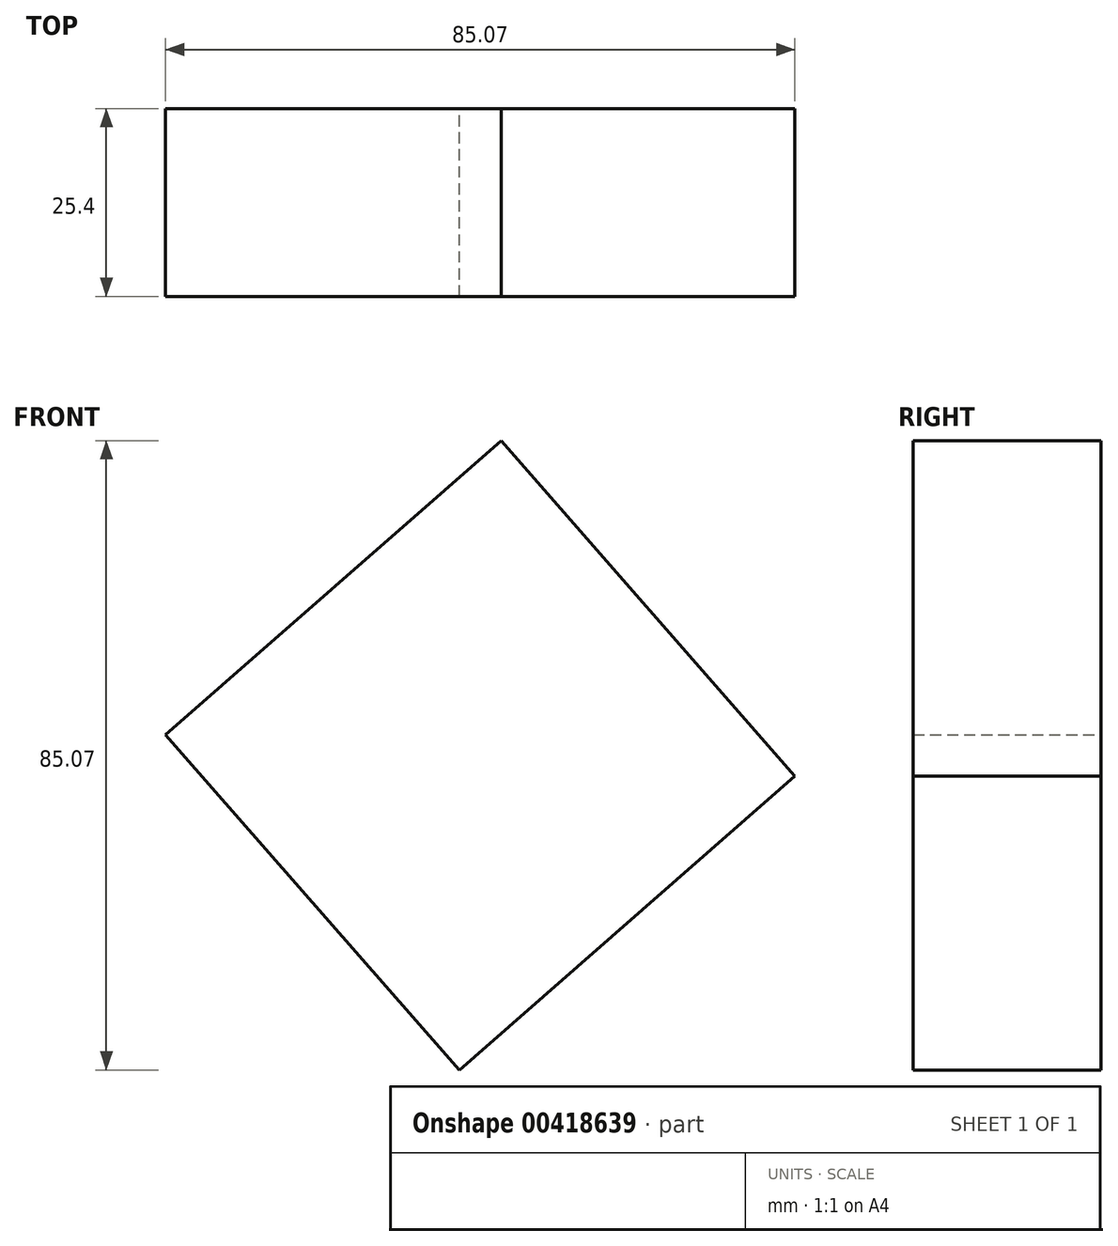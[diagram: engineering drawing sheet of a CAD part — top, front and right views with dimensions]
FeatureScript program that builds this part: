
annotation { "Feature Type Name" : "Feature", "Feature Type Description" : "" }
export const myFeature = defineFeature(function(context is Context, id is Id, definition is map)
    precondition{}
    {
        {
            var Q0;
            Q0=qCreatedBy(makeId("Front.planeOp"),FACE);
            var sketch = newSketch(context, id + "F0", { "sketchPlane" : qUnion([Q0])});
            skCircle(sketch, "E0.cCircle", {"center": v(30.36, 23.23) * mm, "radius": 30.14 * mm, "construction": true});
            skLineSegment(sketch, "E0.0", {"start": v(27.54, -19.3) * mm, "end": v(-12.18, 26.05) * mm});
            skLineSegment(sketch, "E0.1", {"start": v(-12.18, 26.05) * mm, "end": v(33.17, 65.77) * mm});
            skLineSegment(sketch, "E0.2", {"start": v(33.17, 65.77) * mm, "end": v(72.89, 20.42) * mm});
            skLineSegment(sketch, "E0.3", {"start": v(72.89, 20.42) * mm, "end": v(27.54, -19.3) * mm});
            skPoint(sketch, "E0.0.midPoint", {"position": v(7.68, 3.37) * mm});
            skSolve(sketch);
        }
        {
            var Q0;
            Q0=makeQuery(id+"F0.imprint","IMPRINT",FACE,{"disambiguationData":[TD([[makeQuery(id+"F0.imprint","IMPRINT",EDGE,{"derivedFrom":sQuery(id+"F0.wireOp",EDGE,"E0.0")}),-1.0]])]});
            extrude(context, id + "F1", {"entities" : qUnion([Q0]), "depth" : 25.4 * mm});
        }
    });
